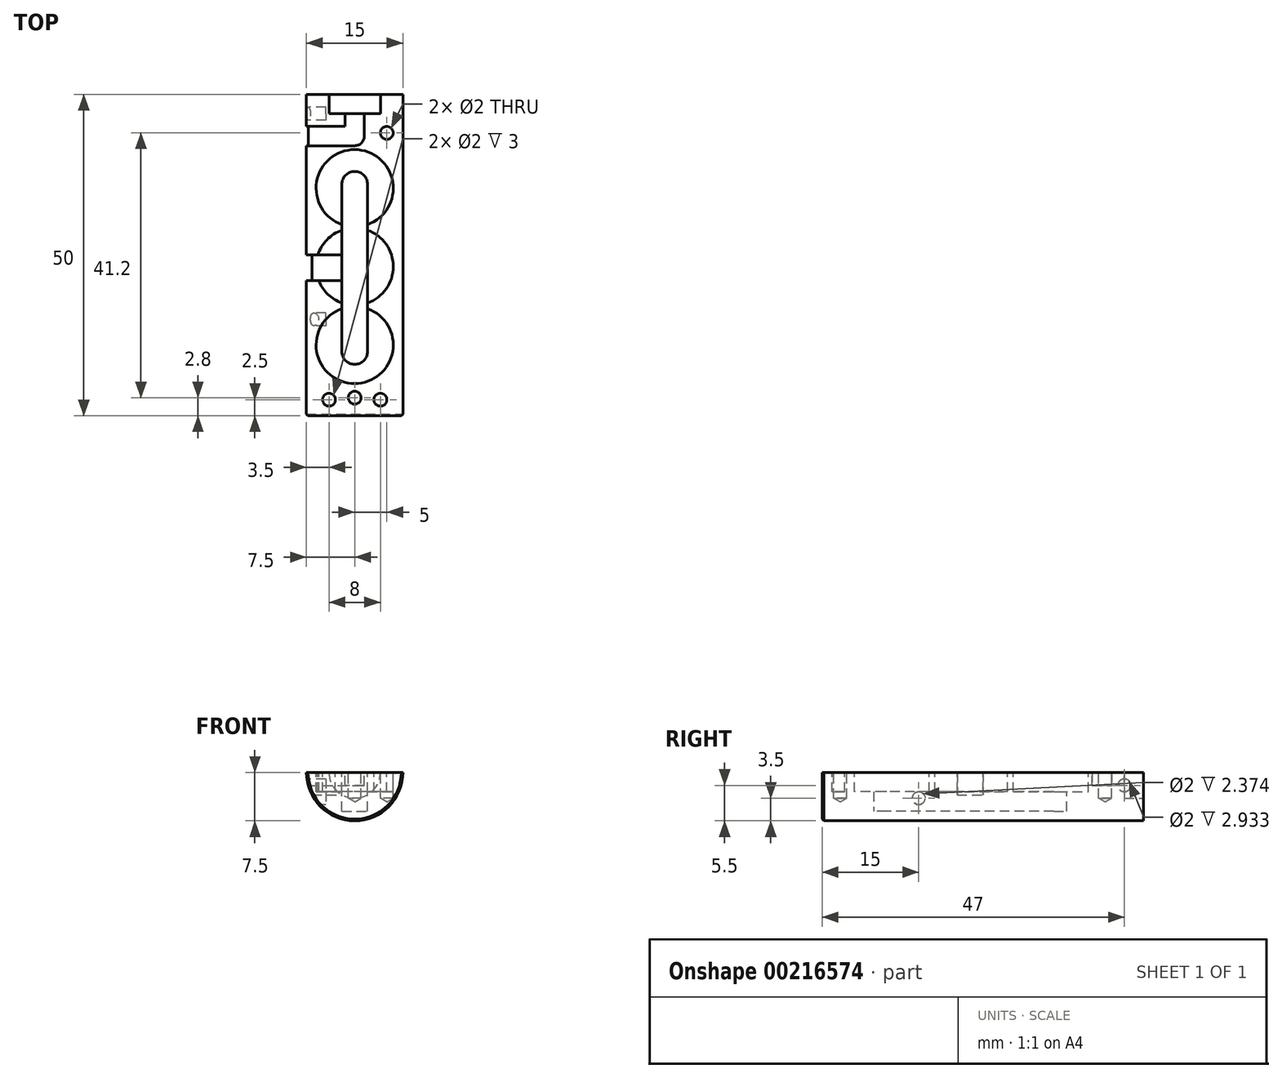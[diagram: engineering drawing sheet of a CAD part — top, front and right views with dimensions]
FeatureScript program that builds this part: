
annotation { "Feature Type Name" : "Feature", "Feature Type Description" : "" }
export const myFeature = defineFeature(function(context is Context, id is Id, definition is map)
    precondition{}
    {
        {
            var Q0;
            Q0=qCreatedBy(makeId("Front.planeOp"),FACE);
            var sketch = newSketch(context, id + "F0", { "sketchPlane" : qUnion([Q0])});
            skArc(sketch, "E0", {"start": v(-7.5, 0) * mm, "mid": v(0, -7.5) * mm, "end": v(7.5, 0) * mm});
            skLineSegment(sketch, "E1", {"start": v(-7.5, 0) * mm, "end": v(7.5, 0) * mm});
            skSolve(sketch);
        }
        {
            var Q0;
            Q0=qSketchRegion(id+"F0",true);
            extrude(context, id + "F1", {"entities" : qUnion([Q0]), "depth" : 50 * mm});
        }
        {
            var Q0;
            Q0=makeQuery(id+"F1.opExtrude","SWEPT_FACE",FACE,{"disambiguationData":[OSD([sQuery(id+"F0.wireOp",EDGE,"E1")])]});
            var sketch = newSketch(context, id + "F2", { "sketchPlane" : qUnion([Q0])});
            skCircle(sketch, "E2", {"center": v(0, -39) * mm, "radius": 6 * mm});
            skCircle(sketch, "E3.0.1.0", {"center": v(0, -26.8) * mm, "radius": 6 * mm});
            skCircle(sketch, "E3.0.2.0", {"center": v(0, -14.6) * mm, "radius": 6 * mm});
            skLineSegment(sketch, "E3.direction1", {"start": v(0, -39) * mm, "end": v(25, -39) * mm, "construction": true});
            skLineSegment(sketch, "E3.direction2", {"start": v(0, -39) * mm, "end": v(0, -26.8) * mm, "construction": true});
            skSolve(sketch);
        }
        {
            var Q0;
            Q0=qSketchRegion(id+"F2",true);
            extrude(context, id + "F3", {"entities" : qUnion([Q0]), "operationType" : NewBodyOperationType.REMOVE, "oppositeDirection" : true, "depth" : 3 * mm});
        }
        {
            var Q0;
            Q0=makeQuery(id+"F1.opExtrude","CAP_FACE",FACE,{"disambiguationData":[OSD([sQuery(id+"F0.wireOp",EDGE,"E0"),sQuery(id+"F0.wireOp",EDGE,"E1")])],"isStart":true});
            var sketch = newSketch(context, id + "F4", { "sketchPlane" : qUnion([Q0])});
            skCircle(sketch, "E4", {"center": v(0, 0) * mm, "radius": 4 * mm});
            skSolve(sketch);
        }
        {
            var Q0;
            Q0=qSketchRegion(id+"F4",true);
            extrude(context, id + "F5", {"entities" : qUnion([Q0]), "operationType" : NewBodyOperationType.REMOVE, "oppositeDirection" : true, "depth" : 3 * mm});
        }
        {
            var Q0;
            Q0=makeQuery(id+"F1.opExtrude","SWEPT_FACE",FACE,{"disambiguationData":[OSD([sQuery(id+"F0.wireOp",EDGE,"E1")])]});
            var sketch = newSketch(context, id + "F6", { "sketchPlane" : qUnion([Q0])});
            skLineSegment(sketch, "E5.bottom", {"start": v(-2, -12) * mm, "end": v(2, -12) * mm});
            skLineSegment(sketch, "E5.top", {"start": v(-2, -42) * mm, "end": v(2, -42) * mm});
            skLineSegment(sketch, "E5.left", {"start": v(-2, -12) * mm, "end": v(-2, -42) * mm});
            skLineSegment(sketch, "E5.right", {"start": v(2, -12) * mm, "end": v(2, -42) * mm});
            skSolve(sketch);
        }
        {
            var Q0;
            Q0 = qSketchRegion(id + "F6", true);
            extrude(context, id + "F7", {"entities" : qUnion([Q0]), "operationType" : NewBodyOperationType.REMOVE, "oppositeDirection" : true, "depth" : 6 * mm});
        }
        {
            var Q0;
            Q0=makeQuery(id+"F7.boolean.opBoolean","COPY",EDGE,{"derivedFrom":makeQuery(id+"F7.opExtrude","SWEPT_EDGE",EDGE,{"disambiguationData":[OSD([sQuery(id+"F6.wireOp",EDGE,"E5.bottom"),sQuery(id+"F6.wireOp",EDGE,"E5.left")])]})});
            var Q1;
            Q1=makeQuery(id+"F7.boolean.opBoolean","COPY",EDGE,{"derivedFrom":makeQuery(id+"F7.opExtrude","SWEPT_EDGE",EDGE,{"disambiguationData":[OSD([sQuery(id+"F6.wireOp",EDGE,"E5.bottom"),sQuery(id+"F6.wireOp",EDGE,"E5.right")])]})});
            var Q2;
            Q2=makeQuery(id+"F7.boolean.opBoolean","COPY",EDGE,{"derivedFrom":makeQuery(id+"F7.opExtrude","SWEPT_EDGE",EDGE,{"disambiguationData":[OSD([sQuery(id+"F6.wireOp",EDGE,"E5.top"),sQuery(id+"F6.wireOp",EDGE,"E5.left")])]})});
            var Q3;
            Q3=makeQuery(id+"F7.boolean.opBoolean","COPY",EDGE,{"derivedFrom":makeQuery(id+"F7.opExtrude","SWEPT_EDGE",EDGE,{"disambiguationData":[OSD([sQuery(id+"F6.wireOp",EDGE,"E5.top"),sQuery(id+"F6.wireOp",EDGE,"E5.right")])]})});
            fillet(context, id + "F8", {"entities" : qUnion([Q0, Q1, Q2, Q3]), "radius" : 2 * mm, "tangentPropagation" : true, "allowEdgeOverflow" : false});
        }
        {
            var Q0;
            Q0=makeQuery(id+"F1.opExtrude","SWEPT_FACE",FACE,{"disambiguationData":[OSD([sQuery(id+"F0.wireOp",EDGE,"E1")])]});
            var sketch = newSketch(context, id + "F9", { "sketchPlane" : qUnion([Q0])});
            skLineSegment(sketch, "E6.bottom", {"start": v(-9.4, -29) * mm, "end": v(0, -29) * mm});
            skLineSegment(sketch, "E6.top", {"start": v(-9.4, -25) * mm, "end": v(0, -25) * mm});
            skLineSegment(sketch, "E6.left", {"start": v(0, -29) * mm, "end": v(0, -25) * mm});
            skLineSegment(sketch, "E6.right", {"start": v(-9.4, -29) * mm, "end": v(-9.4, -25) * mm});
            skSolve(sketch);
        }
        {
            var Q0;
            Q0 = qSketchRegion(id + "F9", true);
            extrude(context, id + "F10", {"entities" : qUnion([Q0]), "operationType" : NewBodyOperationType.REMOVE, "oppositeDirection" : true, "depth" : 3.5 * mm});
        }
        {
            var Q0;
            Q0=makeQuery(id+"F1.opExtrude","SWEPT_FACE",FACE,{"disambiguationData":[OSD([sQuery(id+"F0.wireOp",EDGE,"E1")])]});
            var sketch = newSketch(context, id + "F11", { "sketchPlane" : qUnion([Q0])});
            skPoint(sketch, "E7", {"position": v(0, -47.2) * mm});
            skPoint(sketch, "E8", {"position": v(5, -6) * mm});
            skSolve(sketch);
        }
        {
            var Q0;
            Q0=sQuery(id+"F11.wireOp",VERTEX,"E8");
            var Q1;
            Q1=sQuery(id+"F11.wireOp",VERTEX,"E7");
            var Q2;
            Q2=makeQuery(id+"F1.opExtrude","SWEPT_BODY",BODY,{"disambiguationData":[OSD([sQuery(id+"F0.wireOp",EDGE,"E0"),sQuery(id+"F0.wireOp",EDGE,"E1")])]});
            hole(context, id + "F12", {"style" : HoleStyle.SIMPLE, "endStyle" : HoleEndStyle.BLIND, "holeDiameter" : 2 * mm, "holeDepth" : 4 * mm, "locations" : qUnion([Q0, Q1]), "scope" : qUnion([Q2])});
        }
        {
            var Q0;
            Q0=makeQuery(id+"F1.opExtrude","SWEPT_FACE",FACE,{"disambiguationData":[OSD([sQuery(id+"F0.wireOp",EDGE,"E1")])]});
            var sketch = newSketch(context, id + "F13", { "sketchPlane" : qUnion([Q0])});
            skLineSegment(sketch, "E9.bottom", {"start": v(-1.5, -3) * mm, "end": v(1.5, -3) * mm});
            skLineSegment(sketch, "E9.top", {"start": v(-1.5, -8) * mm, "end": v(1.5, -8) * mm});
            skLineSegment(sketch, "E9.left", {"start": v(-1.5, -3) * mm, "end": v(-1.5, -5) * mm});
            skLineSegment(sketch, "E9.right", {"start": v(1.5, -3) * mm, "end": v(1.5, -8) * mm});
            skLineSegment(sketch, "E10.bottom", {"start": v(-8.88, -5) * mm, "end": v(-1.5, -5) * mm});
            skLineSegment(sketch, "E10.top", {"start": v(-8.88, -8) * mm, "end": v(-1.5, -8) * mm});
            skLineSegment(sketch, "E10.left", {"start": v(-8.88, -5) * mm, "end": v(-8.88, -8) * mm});
            skSolve(sketch);
        }
        {
            var Q0;
            Q0 = qSketchRegion(id + "F13", true);
            extrude(context, id + "F14", {"entities" : qUnion([Q0]), "operationType" : NewBodyOperationType.REMOVE, "oppositeDirection" : true, "depth" : 2 * mm});
        }
        {
            var Q0;
            Q0=makeQuery(id+"F14.boolean.opBoolean","COPY",EDGE,{"derivedFrom":makeQuery(id+"F14.opExtrude","SWEPT_EDGE",EDGE,{"disambiguationData":[OSD([sQuery(id+"F13.wireOp",EDGE,"E9.top"),sQuery(id+"F13.wireOp",EDGE,"E9.right")])]})});
            fillet(context, id + "F15", {"entities" : qUnion([Q0]), "radius" : 1.5 * mm, "tangentPropagation" : true, "allowEdgeOverflow" : false});
        }
        {
            var Q0;
            Q0=makeQuery(id+"F1.opExtrude","CAP_EDGE",EDGE,{"disambiguationData":[OSD([sQuery(id+"F0.wireOp",EDGE,"E0")])],"isStart":false});
            chamfer(context, id + "F16", {"entities" : qUnion([Q0]), "width" : 0.25 * mm, "tangentPropagation" : true});
        }
        {
            var Q0;
            Q0=qCreatedBy(makeId("Right.planeOp"),FACE);
            cPlane(context, id + "F17", {"entities" : qUnion([Q0]), "cplaneType" : CPlaneType.OFFSET, "offset" : 7.5 * mm, "oppositeDirection" : true, "width" : 150 * mm, "height" : 150 * mm});
        }
        {
            var Q0;
            Q0=qCreatedBy(id+"F17.planeOp",FACE);
            var sketch = newSketch(context, id + "F18", { "sketchPlane" : qUnion([Q0])});
            skCircle(sketch, "E11", {"center": v(-3, -2) * mm, "radius": 1 * mm});
            skCircle(sketch, "E12", {"center": v(-35, -4) * mm, "radius": 1 * mm});
            skSolve(sketch);
        }
        {
            var Q0;
            Q0 = qSketchRegion(id + "F18", true);
            extrude(context, id + "F19", {"entities" : qUnion([Q0]), "operationType" : NewBodyOperationType.REMOVE, "depth" : 3 * mm});
        }
        {
            var Q0;
            {var subQ2=sQuery(id+"F0.wireOp",EDGE,"E1");Q0=makeQuery(id+"F14.boolean.opBoolean","SPLIT",FACE,{"disambiguationData":[TD([makeQuery(id+"F3.boolean.opBoolean","COPY",FACE,{"derivedFrom":makeQuery(id+"F3.opExtrude","SWEPT_FACE",FACE,{"disambiguationData":[OSD([sQuery(id+"F2.wireOp",EDGE,"E2")])]})})])],"derivedFrom":makeQuery(id+"F1.opExtrude","SWEPT_FACE",FACE,{"disambiguationData":[OSD([subQ2])]})});}
            var sketch = newSketch(context, id + "F20", { "sketchPlane" : qUnion([Q0])});
            skCircle(sketch, "E13", {"center": v(-4, -47.5) * mm, "radius": 1 * mm});
            skCircle(sketch, "E14", {"center": v(4, -47.5) * mm, "radius": 1 * mm});
            skSolve(sketch);
        }
        {
            var Q0;
            Q0 = qSketchRegion(id + "F20", true);
            extrude(context, id + "F21", {"entities" : qUnion([Q0]), "operationType" : NewBodyOperationType.REMOVE, "oppositeDirection" : true, "depth" : 3 * mm});
        }
    });
